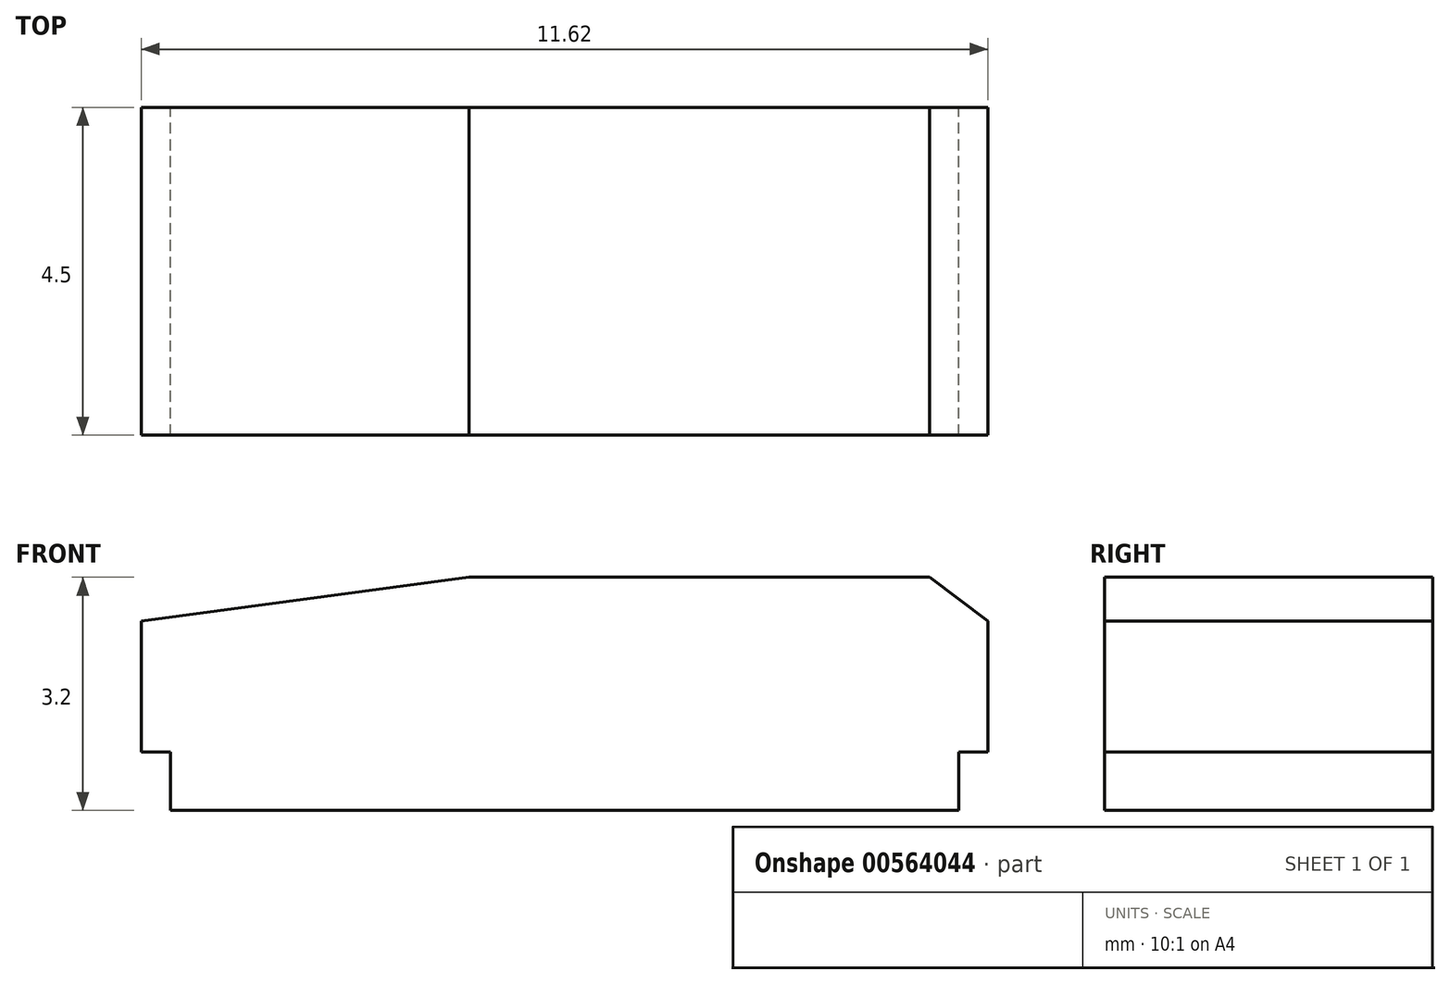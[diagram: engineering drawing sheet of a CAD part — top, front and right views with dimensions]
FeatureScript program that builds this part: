
annotation { "Feature Type Name" : "Feature", "Feature Type Description" : "" }
export const myFeature = defineFeature(function(context is Context, id is Id, definition is map)
    precondition{}
    {
        {
            var Q0;
            Q0=qCreatedBy(makeId("Front.planeOp"),FACE);
            var sketch = newSketch(context, id + "F0", { "sketchPlane" : qUnion([Q0])});
            skLineSegment(sketch, "E0.bottom", {"start": v(-1.3, 2.4) * mm, "end": v(5.01, 2.4) * mm});
            skLineSegment(sketch, "E0.top", {"start": v(-5.81, 0) * mm, "end": v(5.81, 0) * mm});
            skLineSegment(sketch, "E0.left", {"start": v(-5.81, 1.8) * mm, "end": v(-5.81, 0) * mm});
            skLineSegment(sketch, "E0.right", {"start": v(5.81, 1.8) * mm, "end": v(5.81, 0) * mm});
            skPoint(sketch, "E1", {"position": v(0, 0) * mm});
            skPoint(sketch, "E2", {"position": v(-1.3, 2.4) * mm});
            skPoint(sketch, "E3", {"position": v(-5.8, 1.8) * mm});
            skLineSegment(sketch, "E4", {"start": v(-5.8, 1.8) * mm, "end": v(-1.3, 2.4) * mm});
            skPoint(sketch, "E5", {"position": v(5.01, 2.4) * mm});
            skPoint(sketch, "E6", {"position": v(5.81, 1.8) * mm});
            skLineSegment(sketch, "E7", {"start": v(5.81, 1.8) * mm, "end": v(5.01, 2.4) * mm});
            skLineSegment(sketch, "E8.bottom", {"start": v(-5.4, 0) * mm, "end": v(5.41, 0) * mm});
            skLineSegment(sketch, "E8.top", {"start": v(-5.4, -0.8) * mm, "end": v(5.41, -0.8) * mm});
            skLineSegment(sketch, "E8.left", {"start": v(-5.4, 0) * mm, "end": v(-5.4, -0.8) * mm});
            skLineSegment(sketch, "E8.right", {"start": v(5.41, 0) * mm, "end": v(5.41, -0.8) * mm});
            skSolve(sketch);
        }
        {
            var Q0;
            Q0=makeQuery(id+"F0.imprint","IMPRINT",FACE,{"disambiguationData":[TD([[makeQuery(id+"F0.imprint","IMPRINT",EDGE,{"derivedFrom":sQuery(id+"F0.wireOp",EDGE,"E0.bottom")}),-1.0]])]});
            extrude(context, id + "F1", {"entities" : qUnion([Q0]), "flatOperationType" : FlatOperationType.REMOVE, "oppositeDirection" : true, "depth" : 4.5 * mm, "offsetDistance" : 25 * mm, "domain" : OperationDomain.MODEL, "symmetric" : true});
        }
        {
            var Q0;
            Q0=makeQuery(id+"F0.imprint","IMPRINT",FACE,{"disambiguationData":[TD([[makeQuery(id+"F0.imprint","IMPRINT",EDGE,{"derivedFrom":sQuery(id+"F0.wireOp",EDGE,"E8.top")}),1.0]])]});
            extrude(context, id + "F2", {"entities" : qUnion([Q0]), "operationType" : NewBodyOperationType.ADD, "flatOperationType" : FlatOperationType.REMOVE, "depth" : 4.5 * mm, "offsetDistance" : 25 * mm, "domain" : OperationDomain.MODEL, "symmetric" : true});
        }
    });
